# Revit family: S-779
name_source: partatom
category: Aparatos sanitarios
revit_build: Autodesk Revit 2015 (Build: 20140606_1530(x64)
units: mm (PartAtom-declared; Revit-internal decimal feet)

## types (6) — shared parameters
Altura total mínima = 121-131 mm
Caudal = 0.8 L/s
Comentarios de tipo = CON PRENSATELAS PARA LÁMINAS IMPERMEABILIZANTES GEOTEXTILES O DE PVC. CON PROTECCION DE OBRA.  CON REJILLA REGULABLE EN ALTURA.
Descripción = CANALETA PARA PLATOS DE DUCHA DE OBRA, SIFON ORIENTABLE, SALIDA HORIZONTAL ORIENTABLE, CON REJILLA CLASSIC, CON PIES DE REGULACION DE ALTURA
Emax = 16 mm  [stored 0.0524934 ft]
Emin = 6 mm  [stored 0.019685 ft]
Fabricante = Jimten
H_DiámetroExt = 40 mm  [stored 0.131234 ft]
Material = ABS
Modelo = S-779
Rejilla = INOX AISI304
Salida = 40M/50M
Sello hidráulico = 50 mm
URL = http://www.jimten.com
WFU = 1

## per-type parameters (varying)
| type | A_Outlet | B_Rejilla | DistPatas | Medida | Referencia | TipoRejilla |
| 70x650mm_Soft | 700 mm  [stored 2.29659 ft] | 670 mm  [stored 2.19816 ft] | 500 mm  [stored 1.64042 ft] | 650mm x 70mm | 13746 | 10 |
| 70x750mm_Soft | 800 mm  [stored 2.62467 ft] | 770 mm  [stored 2.52625 ft] | 600 mm | 750mm x 70mm | 13747 | 11 |
| 70x850mm_Soft | 900 mm  [stored 2.95276 ft] | 870 mm  [stored 2.85433 ft] | 700 mm  [stored 2.29659 ft] | 850mm x 70mm | 13748 | 13 |
| 70x950mm_Soft | 1000 mm  [stored 3.28084 ft] | 970 mm  [stored 3.18241 ft] | 800 mm  [stored 2.62467 ft] | 950mm x 70mm | 13749 | 14 |
| 70x350mm_Soft | 400 mm  [stored 1.31234 ft] | 370 mm  [stored 1.21391 ft] | 300 mm | 350mm x 70mm | 13743 | 5 |
| 70x550mm_Soft | 600 mm | 570 mm  [stored 1.87008 ft] | 400 mm  [stored 1.31234 ft] | 550mm x 70mm | 13745 | 8 |

note: [stored X ft] marks values corroborated as IEEE doubles in the binary element streams (Revit-internal decimal feet)

## geometry (parser evidence)
native form markers: Blend x3, Sweep x10
no freeform markers — native parametric forms only
